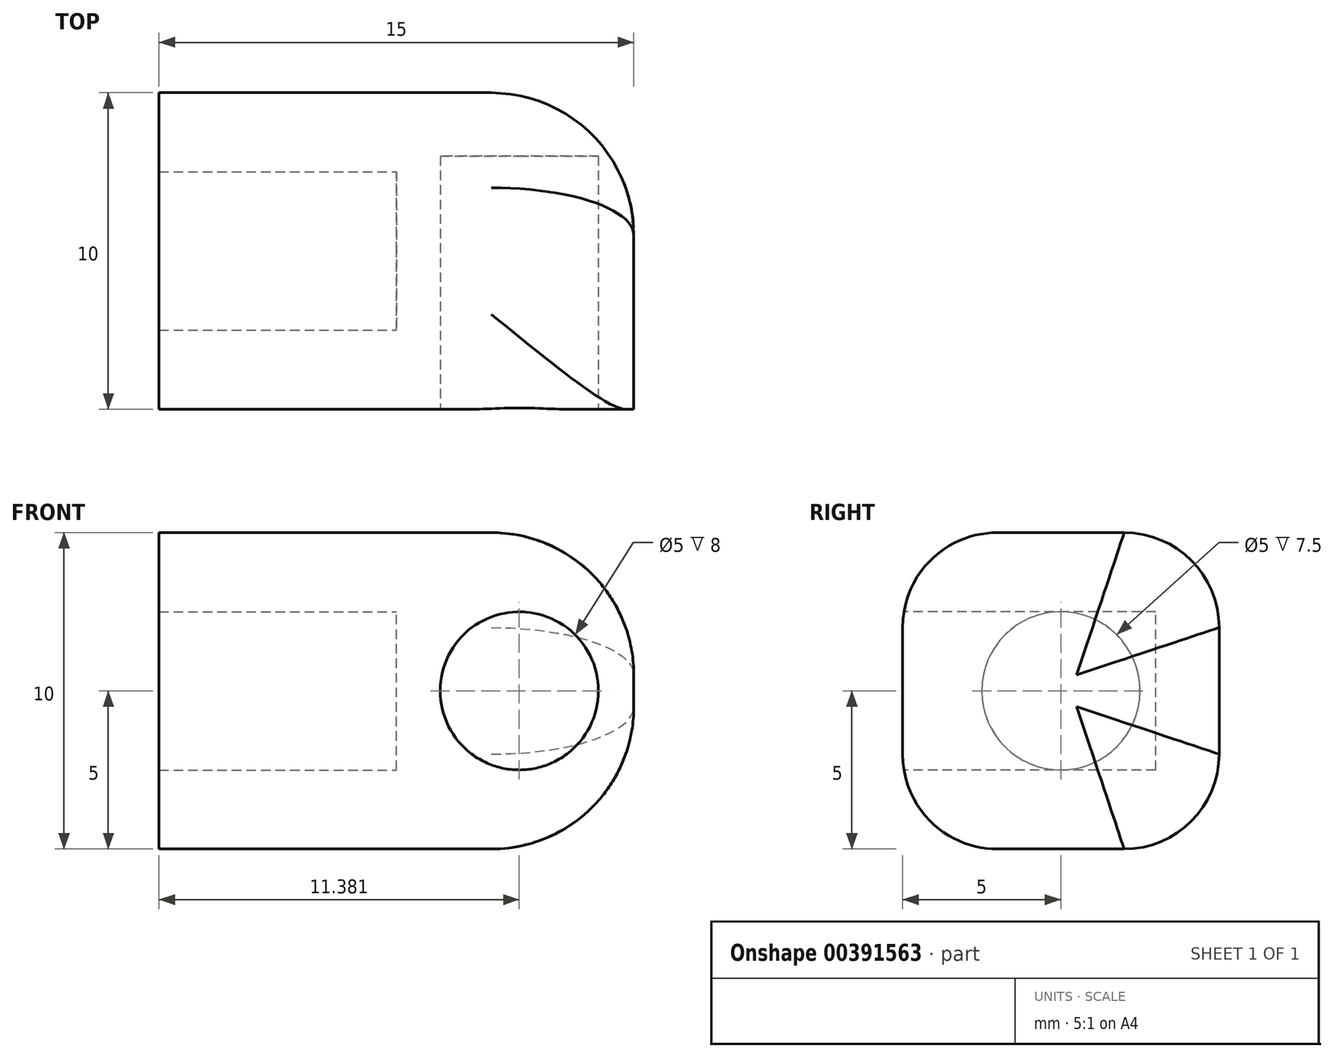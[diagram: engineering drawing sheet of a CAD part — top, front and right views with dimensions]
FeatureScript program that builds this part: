
annotation { "Feature Type Name" : "Feature", "Feature Type Description" : "" }
export const myFeature = defineFeature(function(context is Context, id is Id, definition is map)
    precondition{}
    {
        {
            var Q0;
            Q0=qCreatedBy(makeId("Front.planeOp"),FACE);
            var sketch = newSketch(context, id + "F0", { "sketchPlane" : qUnion([Q0])});
            skLineSegment(sketch, "E0.bottom", {"start": v(-7.5, 0) * mm, "end": v(7.5, 0) * mm});
            skLineSegment(sketch, "E0.top", {"start": v(-7.5, 10) * mm, "end": v(7.5, 10) * mm});
            skLineSegment(sketch, "E0.left", {"start": v(-7.5, 0) * mm, "end": v(-7.5, 10) * mm});
            skLineSegment(sketch, "E0.right", {"start": v(7.5, 0) * mm, "end": v(7.5, 10) * mm});
            skSolve(sketch);
        }
        {
            var Q0;
            Q0=qSketchRegion(id+"F0",true);
            extrude(context, id + "F1", {"entities" : qUnion([Q0]), "depth" : 10 * mm});
        }
        {
            var Q0;
            Q0=makeQuery(id+"F1.opExtrude","CAP_FACE",FACE,{"disambiguationData":[OSD([sQuery(id+"F0.wireOp",EDGE,"E0.bottom"),sQuery(id+"F0.wireOp",EDGE,"E0.top"),sQuery(id+"F0.wireOp",EDGE,"E0.left"),sQuery(id+"F0.wireOp",EDGE,"E0.right")])],"isStart":false});
            var sketch = newSketch(context, id + "F2", { "sketchPlane" : qUnion([Q0])});
            skCircle(sketch, "E1", {"center": v(3.88, 5) * mm, "radius": 2.5 * mm});
            skLineSegment(sketch, "E2", {"start": v(3.88, 10) * mm, "end": v(3.88, 0) * mm, "construction": true});
            skSolve(sketch);
        }
        {
            var Q0;
            Q0=qSketchRegion(id+"F2",true);
            extrude(context, id + "F3", {"entities" : qUnion([Q0]), "operationType" : NewBodyOperationType.REMOVE, "oppositeDirection" : true, "depth" : 8 * mm});
        }
        {
            var Q0;
            Q0=qCreatedBy(makeId("Right.planeOp"),FACE);
            var sketch = newSketch(context, id + "F4", { "sketchPlane" : qUnion([Q0])});
            skCircle(sketch, "E3", {"center": v(-5, 5) * mm, "radius": 2.5 * mm});
            skLineSegment(sketch, "E4", {"start": v(-10, 10) * mm, "end": v(0, 0) * mm, "construction": true});
            skSolve(sketch);
        }
        {
            var Q0;
            Q0=qSketchRegion(id+"F4",true);
            extrude(context, id + "F5", {"entities" : qUnion([Q0]), "operationType" : NewBodyOperationType.REMOVE, "endBound" : BoundingType.THROUGH_ALL, "oppositeDirection" : true, "depth" : 25 * mm});
        }
        {
            var Q0;
            Q0=makeQuery(id+"F1.opExtrude","CAP_EDGE",EDGE,{"disambiguationData":[OSD([sQuery(id+"F0.wireOp",EDGE,"E0.top")])],"isStart":true});
            var Q1;
            Q1=makeQuery(id+"F1.opExtrude","CAP_EDGE",EDGE,{"disambiguationData":[OSD([sQuery(id+"F0.wireOp",EDGE,"E0.top")])],"isStart":false});
            var Q2;
            Q2=makeQuery(id+"F1.opExtrude","CAP_EDGE",EDGE,{"disambiguationData":[OSD([sQuery(id+"F0.wireOp",EDGE,"E0.bottom")])],"isStart":false});
            var Q3;
            Q3=makeQuery(id+"F1.opExtrude","CAP_EDGE",EDGE,{"disambiguationData":[OSD([sQuery(id+"F0.wireOp",EDGE,"E0.bottom")])],"isStart":true});
            fillet(context, id + "F6", {"entities" : qUnion([Q0, Q1, Q2, Q3]), "radius" : 3 * mm, "tangentPropagation" : true, "allowEdgeOverflow" : false});
        }
        {
            var Q0;
            Q0=makeQuery(id+"F1.opExtrude","SWEPT_EDGE",EDGE,{"disambiguationData":[OSD([sQuery(id+"F0.wireOp",EDGE,"E0.top"),sQuery(id+"F0.wireOp",EDGE,"E0.right")])]});
            var Q1;
            Q1=makeQuery(id+"F1.opExtrude","SWEPT_EDGE",EDGE,{"disambiguationData":[OSD([sQuery(id+"F0.wireOp",EDGE,"E0.bottom"),sQuery(id+"F0.wireOp",EDGE,"E0.right")])]});
            var Q2;
            Q2=makeQuery(id+"F1.opExtrude","CAP_EDGE",EDGE,{"disambiguationData":[OSD([sQuery(id+"F0.wireOp",EDGE,"E0.right")])],"isStart":true});
            fillet(context, id + "F7", {"entities" : qUnion([Q0, Q1, Q2]), "radius" : 4.5 * mm, "allowEdgeOverflow" : false});
        }
    });
